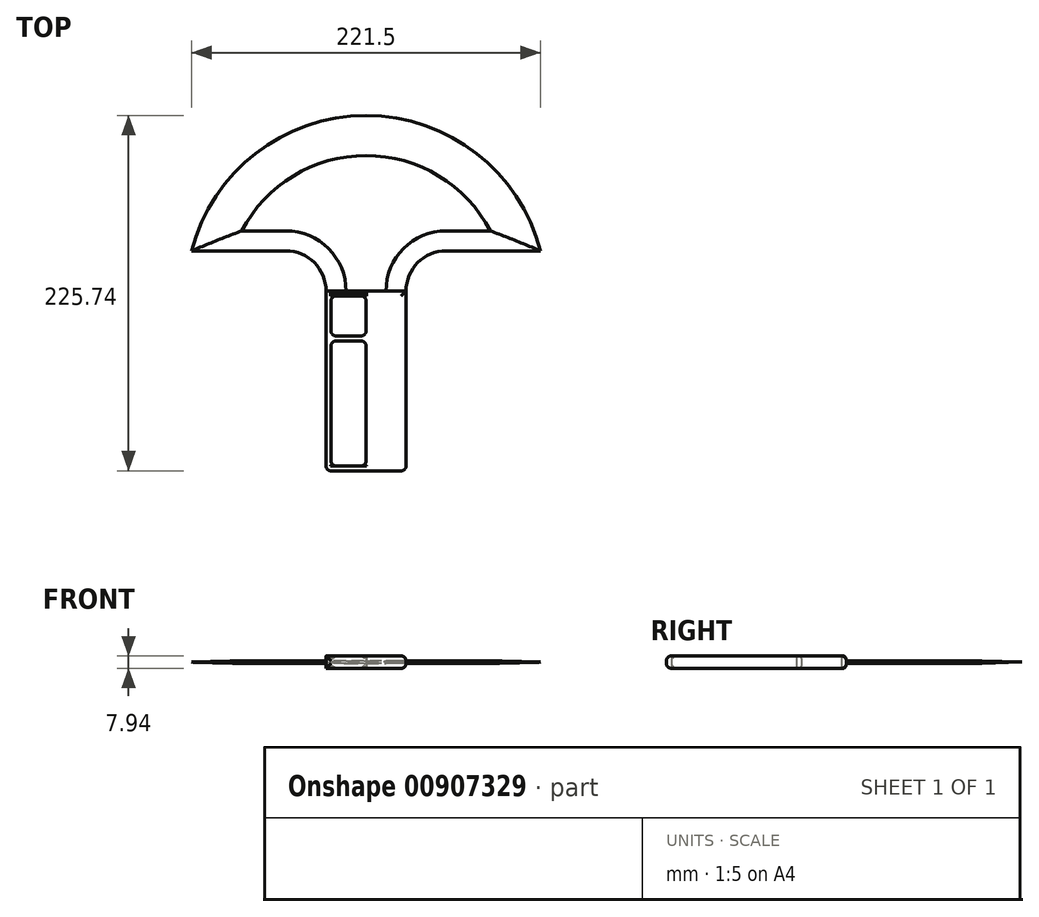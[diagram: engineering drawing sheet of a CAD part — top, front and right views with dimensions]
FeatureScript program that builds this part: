
annotation { "Feature Type Name" : "Feature", "Feature Type Description" : "" }
export const myFeature = defineFeature(function(context is Context, id is Id, definition is map)
    precondition{}
    {
        {
            var Q0;
            Q0=qCreatedBy(makeId("Top.planeOp"),FACE);
            var sketch = newSketch(context, id + "F0", { "sketchPlane" : qUnion([Q0])});
            skArc(sketch, "E0", {"start": v(110.75, 139.7) * mm, "mid": v(0, 225.74) * mm, "end": v(-110.75, 139.7) * mm});
            skLineSegment(sketch, "E1", {"start": v(-25.4, 0) * mm, "end": v(25.4, 0) * mm});
            skLineSegment(sketch, "E2.bottom", {"start": v(-25.4, 0) * mm, "end": v(22.23, 0) * mm});
            skLineSegment(sketch, "E2.top", {"start": v(-25.4, 114.3) * mm, "end": v(25.4, 114.3) * mm});
            skLineSegment(sketch, "E2.left", {"start": v(-25.4, 0) * mm, "end": v(-25.4, 114.3) * mm});
            skLineSegment(sketch, "E2.right", {"start": v(25.4, 3.17) * mm, "end": v(25.4, 114.3) * mm});
            skLineSegment(sketch, "E3.bottom", {"start": v(-3.18, 3.18) * mm, "end": v(-19.05, 3.18) * mm});
            skLineSegment(sketch, "E3.top", {"start": v(-3.18, 82.55) * mm, "end": v(-19.05, 82.55) * mm});
            skLineSegment(sketch, "E3.left", {"start": v(0, 6.35) * mm, "end": v(0, 79.37) * mm});
            skLineSegment(sketch, "E3.right", {"start": v(-22.23, 6.35) * mm, "end": v(-22.23, 79.37) * mm});
            skLineSegment(sketch, "E4.bottom", {"start": v(-3.18, 111.12) * mm, "end": v(-19.05, 111.12) * mm});
            skLineSegment(sketch, "E4.top", {"start": v(-3.18, 85.72) * mm, "end": v(-19.05, 85.72) * mm});
            skLineSegment(sketch, "E4.left", {"start": v(0, 107.95) * mm, "end": v(0, 88.9) * mm});
            skLineSegment(sketch, "E4.right", {"start": v(-22.23, 107.95) * mm, "end": v(-22.23, 88.9) * mm});
            skLineSegment(sketch, "E5", {"start": v(-110.75, 139.7) * mm, "end": v(-50.8, 139.7) * mm});
            skArc(sketch, "E6", {"start": v(50.8, 139.7) * mm, "mid": v(32.84, 132.26) * mm, "end": v(25.4, 114.3) * mm});
            skArc(sketch, "E7", {"start": v(-25.4, 114.3) * mm, "mid": v(-32.84, 132.26) * mm, "end": v(-50.8, 139.7) * mm});
            skLineSegment(sketch, "E8.trimOffspring", {"start": v(50.8, 139.7) * mm, "end": v(110.75, 139.7) * mm});
            skPoint(sketch, "E9.visualSharp", {"position": v(-22.23, 111.12) * mm});
            skArc(sketch, "E9.filletArc", {"start": v(-19.05, 111.12) * mm, "mid": v(-21.3, 110.2) * mm, "end": v(-22.23, 107.95) * mm});
            skPoint(sketch, "E10.visualSharp", {"position": v(0, 111.12) * mm});
            skArc(sketch, "E10.filletArc", {"start": v(0, 107.95) * mm, "mid": v(-0.93, 110.2) * mm, "end": v(-3.18, 111.12) * mm});
            skPoint(sketch, "E11.visualSharp", {"position": v(0, 85.72) * mm});
            skArc(sketch, "E11.filletArc", {"start": v(-3.18, 85.72) * mm, "mid": v(-0.93, 86.65) * mm, "end": v(0, 88.9) * mm});
            skPoint(sketch, "E12.visualSharp", {"position": v(-22.23, 85.72) * mm});
            skArc(sketch, "E12.filletArc", {"start": v(-22.23, 88.9) * mm, "mid": v(-21.3, 86.65) * mm, "end": v(-19.05, 85.72) * mm});
            skPoint(sketch, "E13.visualSharp", {"position": v(-22.23, 82.55) * mm});
            skArc(sketch, "E13.filletArc", {"start": v(-19.05, 82.55) * mm, "mid": v(-21.3, 81.62) * mm, "end": v(-22.23, 79.37) * mm});
            skPoint(sketch, "E14.visualSharp", {"position": v(0, 82.55) * mm});
            skArc(sketch, "E14.filletArc", {"start": v(0, 79.37) * mm, "mid": v(-0.93, 81.62) * mm, "end": v(-3.18, 82.55) * mm});
            skPoint(sketch, "E15.visualSharp", {"position": v(-22.23, 3.18) * mm});
            skArc(sketch, "E15.filletArc", {"start": v(-22.23, 6.35) * mm, "mid": v(-21.3, 4.1) * mm, "end": v(-19.05, 3.18) * mm});
            skPoint(sketch, "E16.visualSharp", {"position": v(0, 3.18) * mm});
            skArc(sketch, "E16.filletArc", {"start": v(-3.18, 3.18) * mm, "mid": v(-0.93, 4.1) * mm, "end": v(0, 6.35) * mm});
            skPoint(sketch, "E17.visualSharp", {"position": v(25.4, 0) * mm});
            skArc(sketch, "E17.filletArc", {"start": v(22.23, 0) * mm, "mid": v(24.47, 0.93) * mm, "end": v(25.4, 3.17) * mm});
            skSolve(sketch);
        }
        {
            var Q0;
            Q0=makeQuery(id+"F0.imprint","IMPRINT",FACE,{"disambiguationData":[TD([[makeQuery(id+"F0.imprint","IMPRINT",EDGE,{"derivedFrom":sQuery(id+"F0.wireOp",EDGE,"E2.top")}),-1.0]])]});
            extrude(context, id + "F1", {"entities" : qUnion([Q0]), "depth" : 3.97 * mm, "offsetDistance" : 25.4 * mm, "hasSecondDirection" : true, "secondDirectionOppositeDirection" : true, "secondDirectionDepth" : 3.97 * mm});
        }
        {
            var Q0;
            Q0=makeQuery(id+"F0.imprint","IMPRINT",FACE,{"disambiguationData":[TD([[makeQuery(id+"F0.imprint","IMPRINT",EDGE,{"derivedFrom":sQuery(id+"F0.wireOp",EDGE,"E0")}),1.0]])]});
            extrude(context, id + "F2", {"entities" : qUnion([Q0]), "operationType" : NewBodyOperationType.ADD, "depth" : 0.8 * mm, "offsetDistance" : 25.4 * mm, "hasSecondDirection" : true, "secondDirectionOppositeDirection" : true, "secondDirectionDepth" : 0.8 * mm});
        }
        {
            var Q0;
            Q0=makeQuery(id+"F2.opExtrude","CAP_EDGE",EDGE,{"disambiguationData":[OSD([sQuery(id+"F0.wireOp",EDGE,"E0")])],"isStart":false});
            chamfer(context, id + "F3", {"entities" : qUnion([Q0]), "chamferType" : ChamferType.TWO_OFFSETS, "width1" : 0.8 * mm, "oppositeDirection" : true, "width2" : 25.4 * mm, "tangentPropagation" : true});
        }
        {
            var Q0;
            Q0=makeQuery(id+"F2.opExtrude","CAP_EDGE",EDGE,{"disambiguationData":[OSD([sQuery(id+"F0.wireOp",EDGE,"E0")])],"isStart":true});
            chamfer(context, id + "F4", {"entities" : qUnion([Q0]), "chamferType" : ChamferType.TWO_OFFSETS, "width1" : 0.8 * mm, "oppositeDirection" : false, "width2" : 25.4 * mm, "tangentPropagation" : true});
        }
        {
            var Q0;
            Q0=makeQuery(id+"F2.opExtrude","CAP_EDGE",EDGE,{"disambiguationData":[OSD([sQuery(id+"F0.wireOp",EDGE,"E8.trimOffspring")])],"isStart":false});
            var Q1;
            Q1=makeQuery(id+"F2.opExtrude","CAP_EDGE",EDGE,{"disambiguationData":[OSD([sQuery(id+"F0.wireOp",EDGE,"E5")])],"isStart":false});
            chamfer(context, id + "F5", {"entities" : qUnion([Q0, Q1]), "chamferType" : ChamferType.TWO_OFFSETS, "width1" : 0.8 * mm, "oppositeDirection" : true, "width2" : 12.7 * mm, "tangentPropagation" : true});
        }
        {
            var Q0;
            Q0=makeQuery(id+"F2.opExtrude","CAP_EDGE",EDGE,{"disambiguationData":[OSD([sQuery(id+"F0.wireOp",EDGE,"E5")])],"isStart":true});
            var Q1;
            Q1=makeQuery(id+"F2.opExtrude","CAP_EDGE",EDGE,{"disambiguationData":[OSD([sQuery(id+"F0.wireOp",EDGE,"E8.trimOffspring")])],"isStart":true});
            chamfer(context, id + "F6", {"entities" : qUnion([Q0, Q1]), "chamferType" : ChamferType.TWO_OFFSETS, "width1" : 0.8 * mm, "oppositeDirection" : false, "width2" : 12.7 * mm, "tangentPropagation" : true});
        }
        {
            var Q0;
            Q0=makeQuery(id+"F1.opExtrude","CAP_EDGE",EDGE,{"disambiguationData":[OSD([sQuery(id+"F0.wireOp",EDGE,"E2.right")])],"isStart":true});
            var Q1;
            Q1=makeQuery(id+"F1.opExtrude","CAP_EDGE",EDGE,{"disambiguationData":[OSD([sQuery(id+"F0.wireOp",EDGE,"E2.right")])],"isStart":false});
            var Q2;
            Q2=makeQuery(id+"F1.opExtrude","CAP_EDGE",EDGE,{"disambiguationData":[OSD([sQuery(id+"F0.wireOp",EDGE,"E1")])],"isStart":true});
            var Q3;
            Q3=makeQuery(id+"F1.opExtrude","CAP_EDGE",EDGE,{"disambiguationData":[OSD([sQuery(id+"F0.wireOp",EDGE,"E1")])],"isStart":false});
            var Q4;
            {var subQ0=sQuery(id+"F0.wireOp",EDGE,"E17.filletArc");var subQ1=sQuery(id+"F0.wireOp",EDGE,"E1");Q4=qUnion([makeQuery(id+"F1.opExtrude","SWEPT_EDGE",EDGE,{"disambiguationData":[OSD([sQuery(id+"F0.wireOp",EDGE,"E2.right"),subQ0])]}),makeQuery(id+"F1.opExtrude","SWEPT_EDGE",EDGE,{"disambiguationData":[OSD([subQ1,sQuery(id+"F0.wireOp",EDGE,"E2.left")])]}),makeQuery(id+"F1.opExtrude","SWEPT_EDGE",EDGE,{"disambiguationData":[OSD([subQ1,subQ0])]})]);}
            fillet(context, id + "F7", {"entities" : qUnion([Q0, Q1, Q2, Q3, Q4]), "radius" : 3.17 * mm, "tangentPropagation" : true, "allowEdgeOverflow" : false});
        }
        {
            var Q0;
            Q0=makeQuery(id+"F1.opExtrude","CAP_EDGE",EDGE,{"disambiguationData":[OSD([sQuery(id+"F0.wireOp",EDGE,"E4.left")])],"isStart":true});
            var Q1;
            Q1=makeQuery(id+"F1.opExtrude","CAP_EDGE",EDGE,{"disambiguationData":[OSD([sQuery(id+"F0.wireOp",EDGE,"E3.left")])],"isStart":true});
            var Q2;
            Q2=makeQuery(id+"F1.opExtrude","CAP_EDGE",EDGE,{"disambiguationData":[OSD([sQuery(id+"F0.wireOp",EDGE,"E4.left")])],"isStart":false});
            var Q3;
            Q3=makeQuery(id+"F1.opExtrude","CAP_EDGE",EDGE,{"disambiguationData":[OSD([sQuery(id+"F0.wireOp",EDGE,"E3.left")])],"isStart":false});
            fillet(context, id + "F8", {"entities" : qUnion([Q0, Q1, Q2, Q3]), "radius" : 1.59 * mm, "tangentPropagation" : true, "allowEdgeOverflow" : false});
        }
        {
            var Q0;
            Q0=makeQuery(id+"F1.opExtrude","CAP_EDGE",EDGE,{"disambiguationData":[OSD([sQuery(id+"F0.wireOp",EDGE,"E2.top")])],"isStart":true});
            var Q1;
            Q1=makeQuery(id+"F1.opExtrude","CAP_EDGE",EDGE,{"disambiguationData":[OSD([sQuery(id+"F0.wireOp",EDGE,"E2.top")])],"isStart":false});
            fillet(context, id + "F9", {"entities" : qUnion([Q0, Q1]), "radius" : 3.17 * mm, "allowEdgeOverflow" : false});
        }
    });
